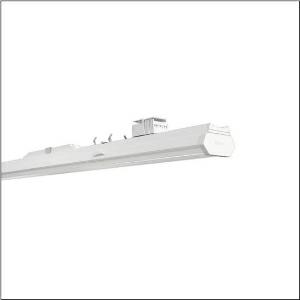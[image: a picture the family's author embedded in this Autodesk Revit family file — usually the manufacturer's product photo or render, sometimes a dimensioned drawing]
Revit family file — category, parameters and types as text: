
# Revit family: licross_r__11_protected_ho_51td11mn4gxs_4279
name_source: partatom
category: Lighting Fixtures
units: mm (PartAtom-declared; Revit-internal decimal feet)

## family parameters
Cut with Voids When Loaded = No
Host = Face
Light Source = No
Part Type = Normal
Room Calculation Point = No
Round Connector Dimension = Use Diameter
Shared = No

## types (1)
- --- (1 x LED, 16070 lm, 87.4 W, 4000K)
    Apparent Load = 87 VA
    CIE Flux Codes = 84 94 98 99 100
    Color Rendering = 80
    Color Temperature = 4000K
    Default Elevation = 1800 mm
    Description = Licross® 11 Protected HO, luminaire insert, of sheet steel, galvanised, coil coated, white, length: 1.500mm, width: 90mm, height: 101mm, LED rated luminous flux: 16.070lm, light colour: 840, control gear: ON/OFF Multilumen, with plug, 3-pole, with phase selection, mains connection: 220..240V, AC, 50/60Hz, rated input power: 87W, halogen-free wiring, primary light control with lens, of plastic, primary optical cover: cover, of PMMA, light emission: direct distribution, primary light characteristic: symmetric, protection rating (complete): IP54, insulation class (complete): insulation class I (protective earthing), certification: CE, ENEC, VDE, UKCA, protection symbol: D if used in an environment with non-conductive dust loads with corresponding accessories, impact resistance: IK06, permissible ambient temperature for indoor applications: -35..+35°C, corresponds to IFS (International Featured Standards) requirements for safety and quality in the food industry, reducing of maximum allowable ambient temperature of 5°C with ceiling mounting, LABS conformity tested according to VDMA 24364:2018-05, packaging unit: 1 piece
    Height = 92 mm
    Lamp = 1 x LED
    Lamp Light Flux = 16070 lm
    Lamp Power = 87.4 W
    Lamp count = 1
    Length = 1500 mm
    Luminous efficacy = 184 lm/W
    Manufacturer = Siteco
    ModVariant = No
    Model = 51TD11MN4GXS
    Mounting Place = Ceiling
    Mounting Type = Pendant
    Number of Poles = 1
    OnlyDefault = Yes
    Power Factor = 1
    Product Name = Licross® 11 Protected HO
    Product group = luminaire insert
    ProductGroupID = 902
    Protection Class = Protection class I
    Protection Degree = IP 54
    RLX_Detail_Level = 1
    RLX_Emergency_Light_Flux = 0 lm
    RLX_Emergency_Type = 0
    RLX_Emergency_Type_DB = No
    RlxData = <blob elided: 22037 chars, md5=b45fe814>
    Socket = socket
    Standby Power = 0 W
    System Light Flux = 16070 lm
    System Power = 87 W
    Type Comments = factory setting: luminous flux: 100 % | (A | C | E) | 203 mA
    Type Image = l_1256145.jpg
    URL = http://relux.com
    VarID = @adj_085856
    Voltage = 0 V
    Weight = 0.00 kg
    Width = 88 mm

## geometry (parser evidence)
native form markers: Blend x4, Sweep x11
no freeform markers — native parametric forms only
